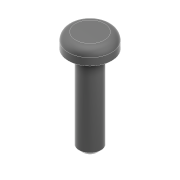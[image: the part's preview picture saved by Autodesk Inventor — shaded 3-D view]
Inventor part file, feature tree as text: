
AUTODESK INVENTOR PART (.ipt)
format: ipt  version: 2022 (Build 260153000, 153)  size: 107,008 bytes
history: native  units: mm
features: extrude x2, sketch x2, chamfer x1, fillet x1
ambient origin geometry x8: Origin, YZ Plane, XZ Plane, XY Plane, X Axis, Y Axis, Z Axis, Center Point
bodies: Solid1 (feature_tree)
feature tree (6):
  extrude  "Extrusion1"  Depth=2.0mm TaperAngle=0.0deg
  extrude  "Extrusion2"  Depth=12.0mm TaperAngle=0.0deg
  chamfer  "Chamfer1"  Distance=2.0mm Angle=45.0deg
  fillet  "Fillet1"  Radius=1.0mm
  sketch  "Sketch1"  dims[d0=6.0mm d1=2.0mm d2=0.0mm]
  sketch  "Sketch2"  dims[d3=3.0mm d4=12.0mm d5=0.0mm d6=0.5mm d7=2.0mm d8=45.0deg d9=1.0mm]
